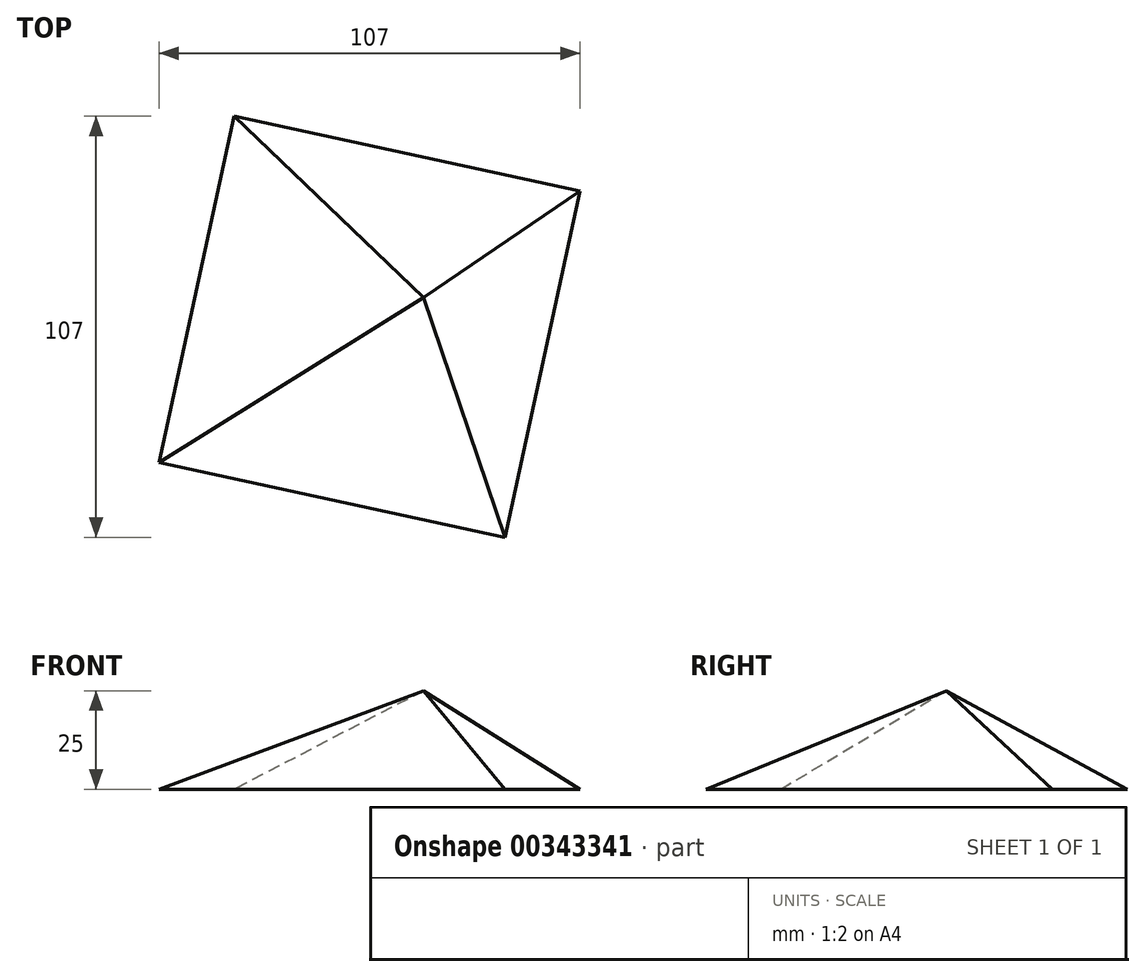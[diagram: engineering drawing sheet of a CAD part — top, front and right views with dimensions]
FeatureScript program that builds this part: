
annotation { "Feature Type Name" : "Feature", "Feature Type Description" : "" }
export const myFeature = defineFeature(function(context is Context, id is Id, definition is map)
    precondition{}
    {
        {
            var Q0;
            Q0=qCreatedBy(makeId("Top.planeOp"),FACE);
            var sketch = newSketch(context, id + "F0", { "sketchPlane" : qUnion([Q0])});
            skCircle(sketch, "E0.cCircle", {"center": v(0, 0) * mm, "radius": 63.62 * mm, "construction": true});
            skLineSegment(sketch, "E0.0", {"start": v(-34.43, 53.5) * mm, "end": v(53.5, 34.43) * mm});
            skLineSegment(sketch, "E0.1", {"start": v(53.5, 34.43) * mm, "end": v(34.43, -53.5) * mm});
            skLineSegment(sketch, "E0.2", {"start": v(34.43, -53.5) * mm, "end": v(-53.5, -34.43) * mm});
            skLineSegment(sketch, "E0.3", {"start": v(-53.5, -34.43) * mm, "end": v(-34.43, 53.5) * mm});
            skSolve(sketch);
        }
        {
            var Q0;
            Q0=qCreatedBy(makeId("Top.planeOp"),FACE);
            cPlane(context, id + "F1", {"entities" : qUnion([Q0]), "cplaneType" : CPlaneType.OFFSET, "offset" : 25 * mm, "width" : 150 * mm, "height" : 150 * mm});
        }
        {
            var Q0;
            Q0=qCreatedBy(id+"F1.planeOp",FACE);
            var sketch = newSketch(context, id + "F2", { "sketchPlane" : qUnion([Q0])});
            skLineSegment(sketch, "E1.bottom", {"start": v(-29.65, -29.02) * mm, "end": v(57, -29.02) * mm});
            skLineSegment(sketch, "E1.top", {"start": v(-29.65, 44) * mm, "end": v(57, 44) * mm});
            skLineSegment(sketch, "E1.left", {"start": v(-29.65, -29.02) * mm, "end": v(-29.65, 44) * mm});
            skLineSegment(sketch, "E1.right", {"start": v(57, -29.02) * mm, "end": v(57, 44) * mm});
            skPoint(sketch, "E1.middle", {"position": v(13.67, 7.49) * mm});
            skSolve(sketch);
        }
        {
            var Q0;
            Q0=sQuery(id+"F2.wireOp",VERTEX,"E1.middle");
            var Q1;
            Q1=makeQuery(id+"F0.imprint","IMPRINT",FACE,{"disambiguationData":[TD([[makeQuery(id+"F0.imprint","IMPRINT",EDGE,{"derivedFrom":sQuery(id+"F0.wireOp",EDGE,"E0.0")}),-1.0]])]});
            loft(context, id + "F3", {"sheetProfilesArray" : [{ "sheetProfileEntities" : qUnion([Q0]) }, { "sheetProfileEntities" : qUnion([Q1]) }]});
        }
    });
